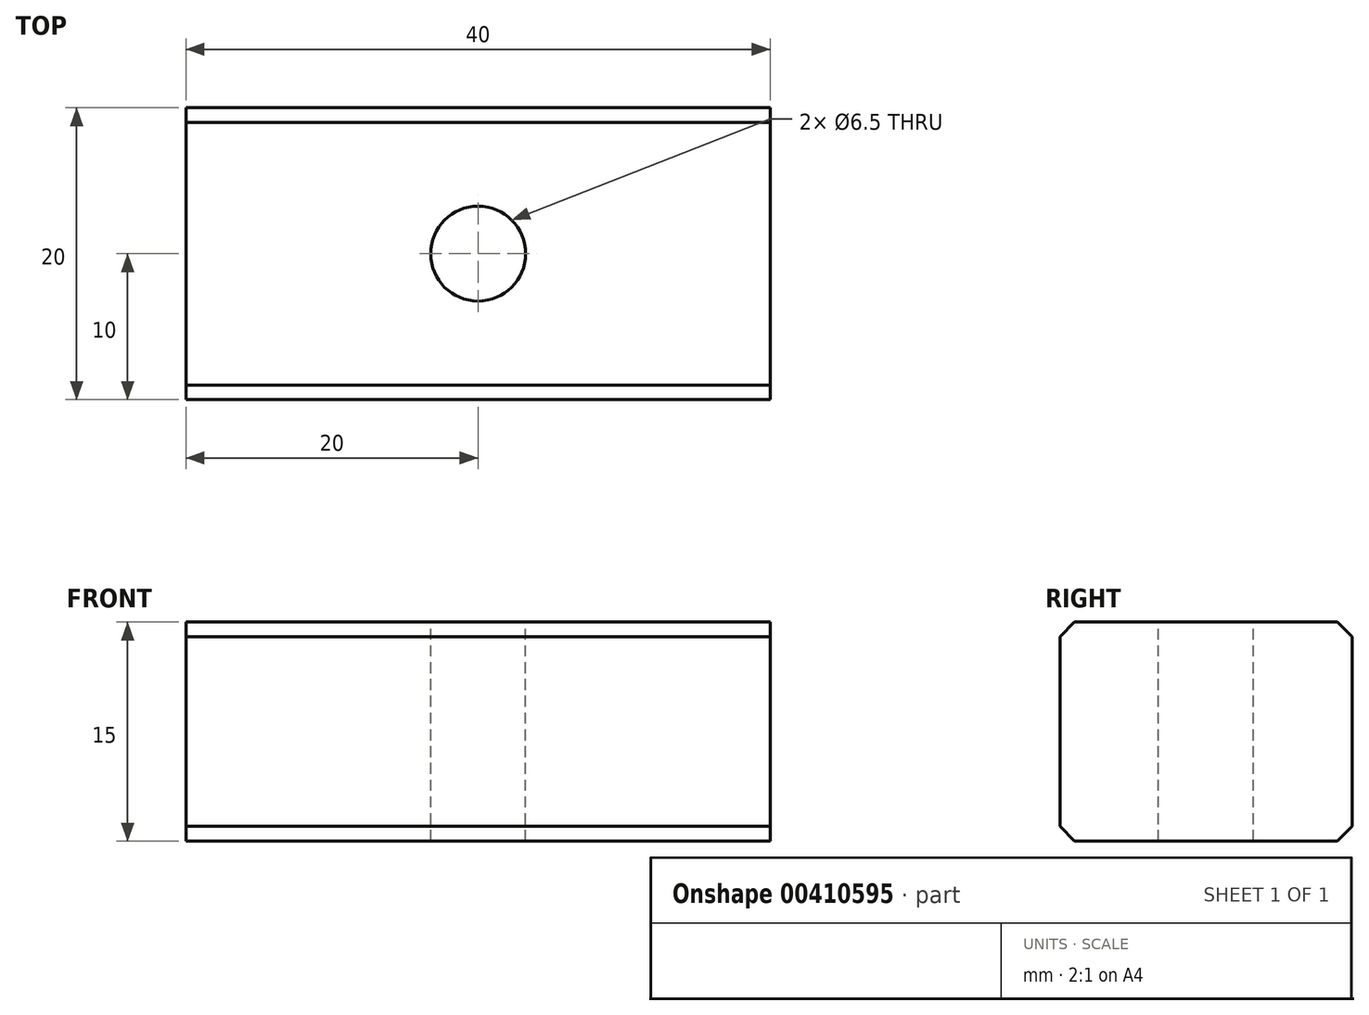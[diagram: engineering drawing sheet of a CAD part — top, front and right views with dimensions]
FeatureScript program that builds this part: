
annotation { "Feature Type Name" : "Feature", "Feature Type Description" : "" }
export const myFeature = defineFeature(function(context is Context, id is Id, definition is map)
    precondition{}
    {
        {
            var Q0;
            Q0=qCreatedBy(makeId("Top.planeOp"),FACE);
            var sketch = newSketch(context, id + "F0", { "sketchPlane" : qUnion([Q0])});
            skLineSegment(sketch, "E0.bottom", {"start": v(0, 0) * mm, "end": v(40, 0) * mm});
            skLineSegment(sketch, "E0.top", {"start": v(0, 20) * mm, "end": v(40, 20) * mm});
            skLineSegment(sketch, "E0.left", {"start": v(0, 0) * mm, "end": v(0, 20) * mm});
            skLineSegment(sketch, "E0.right", {"start": v(40, 0) * mm, "end": v(40, 20) * mm});
            skSolve(sketch);
        }
        {
            var Q0;
            Q0 = qSketchRegion(id + "F0", true);
            extrude(context, id + "F1", {"entities" : qUnion([Q0]), "depth" : 15 * mm});
        }
        {
            var Q0;
            Q0=makeQuery(id+"F1.opExtrude","CAP_FACE",FACE,{"disambiguationData":[OSD([sQuery(id+"F0.wireOp",EDGE,"E0.bottom"),sQuery(id+"F0.wireOp",EDGE,"E0.top"),sQuery(id+"F0.wireOp",EDGE,"E0.left"),sQuery(id+"F0.wireOp",EDGE,"E0.right")])],"isStart":false});
            var sketch = newSketch(context, id + "F2", { "sketchPlane" : qUnion([Q0])});
            skPoint(sketch, "E1", {"position": v(20, 10) * mm});
            skSolve(sketch);
        }
        {
            var Q0;
            Q0=sQuery(id+"F2.wireOp",VERTEX,"E1");
            var Q1;
            Q1=makeQuery(id+"F1.opExtrude","SWEPT_BODY",BODY,{"disambiguationData":[OSD([sQuery(id+"F0.wireOp",EDGE,"E0.bottom"),sQuery(id+"F0.wireOp",EDGE,"E0.top"),sQuery(id+"F0.wireOp",EDGE,"E0.left"),sQuery(id+"F0.wireOp",EDGE,"E0.right")])]});
            hole(context, id + "F3", {"style" : HoleStyle.SIMPLE, "endStyle" : HoleEndStyle.THROUGH, "standardTappedOrClearance" : lookupTablePath({ "standard" : "ISO", "size" : "6.5", "type" : "Drilled" }), "standardBlindInLast" : lookupTablePath({ "standard" : "ISO", "size" : "6.5", "type" : "Drilled" }), "holeDiameter" : 6.5 * mm, "isTappedThrough" : true, "tappedDepth" : 5.6 * mm, "tapClearance" : 3, "locations" : qUnion([Q0]), "scope" : qUnion([Q1])});
        }
        {
            var Q0;
            Q0=makeQuery(id+"F1.opExtrude","CAP_EDGE",EDGE,{"disambiguationData":[OSD([sQuery(id+"F0.wireOp",EDGE,"E0.bottom")])],"isStart":false});
            var Q1;
            Q1=makeQuery(id+"F1.opExtrude","CAP_EDGE",EDGE,{"disambiguationData":[OSD([sQuery(id+"F0.wireOp",EDGE,"E0.top")])],"isStart":false});
            chamfer(context, id + "F4", {"entities" : qUnion([Q0, Q1]), "width" : 1 * mm, "tangentPropagation" : true});
        }
        {
            var Q0;
            Q0=makeQuery(id+"F1.opExtrude","CAP_EDGE",EDGE,{"disambiguationData":[OSD([sQuery(id+"F0.wireOp",EDGE,"E0.bottom")])],"isStart":true});
            var Q1;
            Q1=makeQuery(id+"F1.opExtrude","CAP_EDGE",EDGE,{"disambiguationData":[OSD([sQuery(id+"F0.wireOp",EDGE,"E0.top")])],"isStart":true});
            chamfer(context, id + "F5", {"entities" : qUnion([Q0, Q1]), "width" : 1 * mm, "tangentPropagation" : true});
        }
    });
